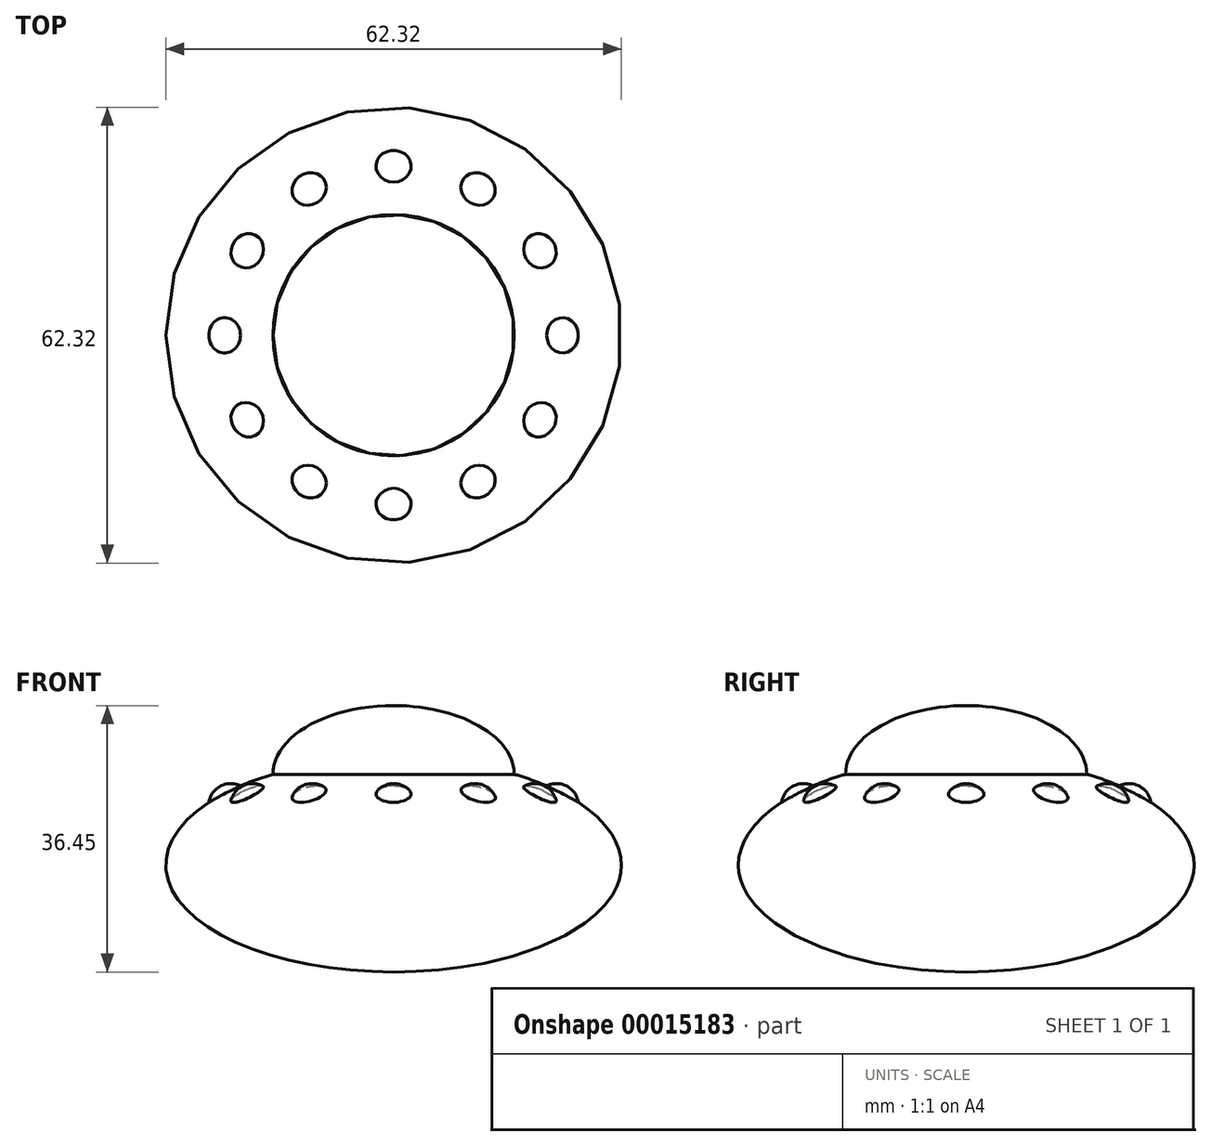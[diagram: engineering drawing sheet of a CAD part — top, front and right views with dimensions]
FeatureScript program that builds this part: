
annotation { "Feature Type Name" : "Feature", "Feature Type Description" : "" }
export const myFeature = defineFeature(function(context is Context, id is Id, definition is map)
    precondition{}
    {
        {
            var Q0;
            Q0=qCreatedBy(makeId("Top.planeOp"),FACE);
            var sketch = newSketch(context, id + "F0", { "sketchPlane" : qUnion([Q0])});
            skEllipticalArc(sketch, "E0", {});
            skEllipticalArc(sketch, "E1", {});
            skLineSegment(sketch, "E2", {"start": v(0, 21.81) * mm, "end": v(0, -14.63) * mm});
            const initialGuessF0  = {"E0": [0, 0, -1, 0, 0.031160544604063034, 0.014632992831229097, 5.270411384881656, 4.154366575887724], "E1": [0, 0.012413225253335453, -1, 0, 0.016499808519058176, 0.009399155969508823, 3.141592653589793, 0]};
            skSetInitialGuess(sketch, initialGuessF0);
            skSolve(sketch);
        }
        {
            var Q0;
            {var subQ0=sQuery(id+"F0.wireOp",EDGE,"E2");Q0=makeQuery(id+"F0.imprint","IMPRINT",FACE,{"disambiguationData":[TD([[makeQuery(id+"F0.imprint","IMPRINT",EDGE,{"derivedFrom":subQ0}),-1.0]])]});}
            var Q1;
            Q1=sQuery(id+"F0.wireOp",EDGE,"E2");
            revolve(context, id + "F1", {"entities" : qUnion([Q0]), "axis" : qUnion([Q1]), "revolveType" : RevolveType.FULL});
        }
        {
            var Q0;
            Q0=qCreatedBy(makeId("Right.planeOp"),FACE);
            var sketch = newSketch(context, id + "F2", { "sketchPlane" : qUnion([Q0])});
            skCircle(sketch, "E3", {"center": v(8.1, -22.26) * mm, "radius": 3.05 * mm});
            skLineSegment(sketch, "E4", {"start": v(8.1, -22.26) * mm, "end": v(11.14, -22.26) * mm});
            skLineSegment(sketch, "E5", {"start": v(8.1, -22.26) * mm, "end": v(5.04, -22.26) * mm});
            skSolve(sketch);
        }
        {
            var Q0;
            {var subQ1=sQuery(id+"F2.wireOp",EDGE,"E4");Q0=makeQuery(id+"F2.imprint","IMPRINT",FACE,{"disambiguationData":[TD([[makeQuery(id+"F2.imprint","IMPRINT",EDGE,{"derivedFrom":subQ1}),1.0]])]});}
            var Q1;
            Q1=sQuery(id+"F2.wireOp",EDGE,"E4");
            revolve(context, id + "F3", {"entities" : qUnion([Q0]), "axis" : qUnion([Q1]), "revolveType" : RevolveType.FULL});
        }
        {
            var Q0;
            Q0=makeQuery(id+"F3.opRevolve","SWEPT_BODY",BODY,{"disambiguationData":[OSD([sQuery(id+"F2.wireOp",EDGE,"E3"),sQuery(id+"F2.wireOp",EDGE,"E4"),sQuery(id+"F2.wireOp",EDGE,"E5")])]});
            var Q1;
            Q1=makeQuery(id+"F1.opRevolve","SWEPT_FACE",FACE,{"disambiguationData":[OSD([sQuery(id+"F0.wireOp",EDGE,"E0")])]});
            circularPattern(context, id + "F4", {"operationType" : NewBodyOperationType.ADD, "entities" : qUnion([Q0]), "axis" : qUnion([Q1]), "angle" : 360 * degree, "instanceCount" : 12, "equalSpace" : true});
        }
        {
            var Q0;
            Q0=makeQuery(id+"F1.opRevolve","SWEPT_BODY",BODY,{"disambiguationData":[OSD([sQuery(id+"F0.wireOp",EDGE,"E0"),sQuery(id+"F0.wireOp",EDGE,"E1"),sQuery(id+"F0.wireOp",EDGE,"E2")])]});
            var Q1;
            Q1=sQuery(id+"F2.wireOp",EDGE,"E3");
            transform(context, id + "F5", {"entities" : qUnion([Q0]), "transformType" : TransformType.ROTATION, "transformAxis" : qUnion([Q1]), "angle" : 90 * degree, "makeCopy" : false});
        }
        {
            var Q0;
            Q0=makeQuery(id+"F1.opRevolve","SWEPT_BODY",BODY,{"disambiguationData":[OSD([sQuery(id+"F0.wireOp",EDGE,"E0"),sQuery(id+"F0.wireOp",EDGE,"E1"),sQuery(id+"F0.wireOp",EDGE,"E2")])]});
            var Q1;
            Q1=qCreatedBy(makeId("Origin.pointOp"),VERTEX);
            var Q2;
            Q2=sQuery(id+"F2.wireOp",VERTEX,"E4.start");
            transform(context, id + "F6", {"entities" : qUnion([Q0]), "transformType" : TransformType.TRANSLATION_ENTITY, "oppositeDirectionEntity" : true, "transformLine" : qUnion([Q1, Q2]), "makeCopy" : false});
        }
        {
            var Q0;
            Q0=makeQuery(id+"F1.opRevolve","SWEPT_BODY",BODY,{"disambiguationData":[OSD([sQuery(id+"F0.wireOp",EDGE,"E0"),sQuery(id+"F0.wireOp",EDGE,"E1"),sQuery(id+"F0.wireOp",EDGE,"E2")])]});
            var Q1;
            Q1=sQuery(id+"F0.wireOp",VERTEX,"E2.end");
            var Q2;
            Q2=qCreatedBy(makeId("Origin.pointOp"),VERTEX);
            transform(context, id + "F7", {"entities" : qUnion([Q0]), "transformType" : TransformType.TRANSLATION_ENTITY, "oppositeDirectionEntity" : false, "transformLine" : qUnion([Q1, Q2]), "makeCopy" : false});
        }
    });
